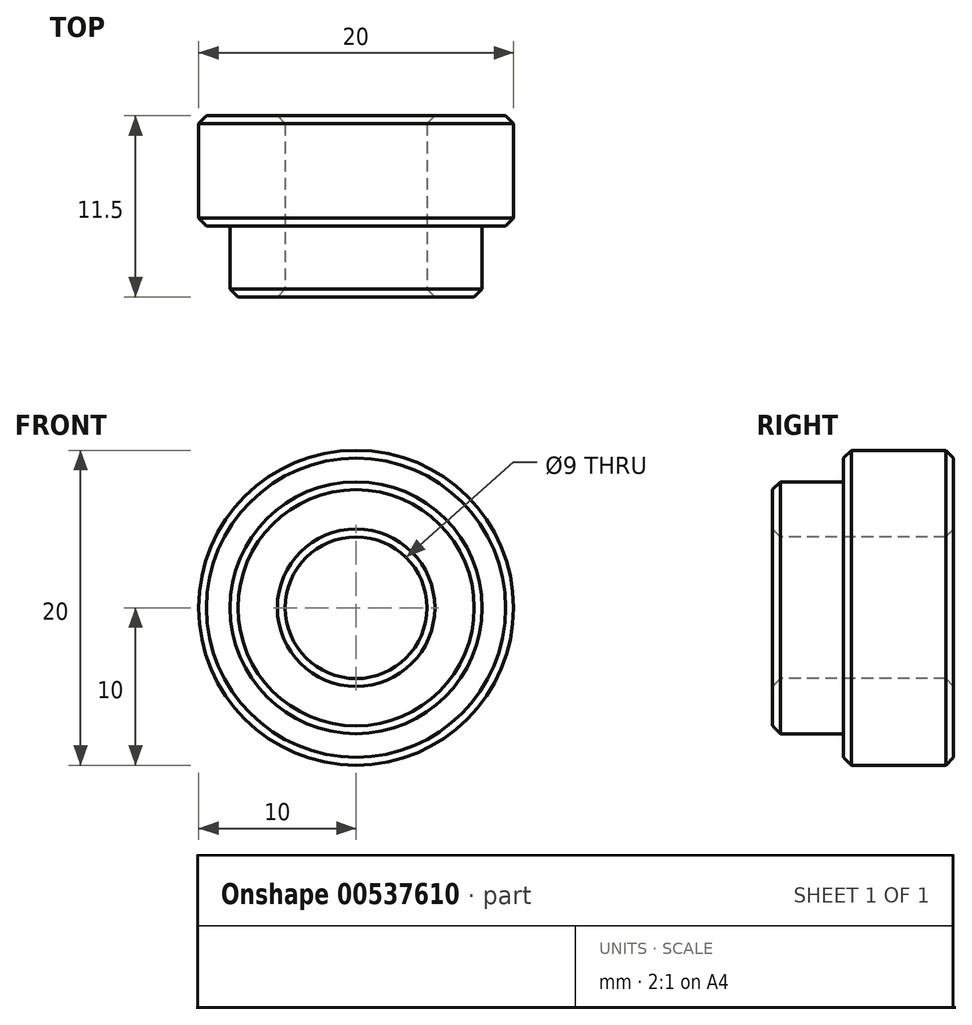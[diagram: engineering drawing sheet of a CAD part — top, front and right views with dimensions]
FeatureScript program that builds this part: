
annotation { "Feature Type Name" : "Feature", "Feature Type Description" : "" }
export const myFeature = defineFeature(function(context is Context, id is Id, definition is map)
    precondition{}
    {
        {
            var Q0;
            Q0=qCreatedBy(makeId("Right.planeOp"),FACE);
            var sketch = newSketch(context, id + "F0", { "sketchPlane" : qUnion([Q0])});
            skLineSegment(sketch, "E0", {"start": v(0, 8) * mm, "end": v(4.5, 8) * mm});
            skLineSegment(sketch, "E1", {"start": v(4.5, 8) * mm, "end": v(4.5, 10) * mm});
            skLineSegment(sketch, "E2", {"start": v(4.5, 10) * mm, "end": v(11.5, 10) * mm});
            skLineSegment(sketch, "E3", {"start": v(11.5, 10) * mm, "end": v(11.5, 4.5) * mm});
            skLineSegment(sketch, "E4", {"start": v(11.5, 4.5) * mm, "end": v(0, 4.5) * mm});
            skLineSegment(sketch, "E5", {"start": v(0, 4.5) * mm, "end": v(0, 8) * mm});
            skLineSegment(sketch, "E6", {"start": v(0, 0) * mm, "end": v(27.42, 0) * mm});
            skSolve(sketch);
        }
        {
            var Q0;
            Q0=makeQuery(id+"F0.imprint","IMPRINT",FACE,{"disambiguationData":[TD([[makeQuery(id+"F0.imprint","IMPRINT",EDGE,{"derivedFrom":sQuery(id+"F0.wireOp",EDGE,"E0")}),-1.0]])]});
            var Q1;
            Q1=sQuery(id+"F0.wireOp",EDGE,"E6");
            revolve(context, id + "F1", {"entities" : qUnion([Q0]), "axis" : qUnion([Q1]), "revolveType" : RevolveType.FULL});
        }
        {
            var Q0;
            Q0=makeQuery(id+"F1.opRevolve","SWEPT_EDGE",EDGE,{"disambiguationData":[OSD([sQuery(id+"F0.wireOp",EDGE,"E3"),sQuery(id+"F0.wireOp",EDGE,"E4")])]});
            var Q1;
            Q1=makeQuery(id+"F1.opRevolve","SWEPT_EDGE",EDGE,{"disambiguationData":[OSD([sQuery(id+"F0.wireOp",EDGE,"E4"),sQuery(id+"F0.wireOp",EDGE,"E5")])]});
            var Q2;
            Q2=makeQuery(id+"F1.opRevolve","SWEPT_EDGE",EDGE,{"disambiguationData":[OSD([sQuery(id+"F0.wireOp",EDGE,"E1"),sQuery(id+"F0.wireOp",EDGE,"E2")])]});
            var Q3;
            Q3=makeQuery(id+"F1.opRevolve","SWEPT_EDGE",EDGE,{"disambiguationData":[OSD([sQuery(id+"F0.wireOp",EDGE,"E2"),sQuery(id+"F0.wireOp",EDGE,"E3")])]});
            var Q4;
            Q4=makeQuery(id+"F1.opRevolve","SWEPT_EDGE",EDGE,{"disambiguationData":[OSD([sQuery(id+"F0.wireOp",EDGE,"E0"),sQuery(id+"F0.wireOp",EDGE,"E5")])]});
            chamfer(context, id + "F2", {"entities" : qUnion([Q0, Q1, Q2, Q3, Q4]), "width" : 0.5 * mm, "tangentPropagation" : true});
        }
    });
